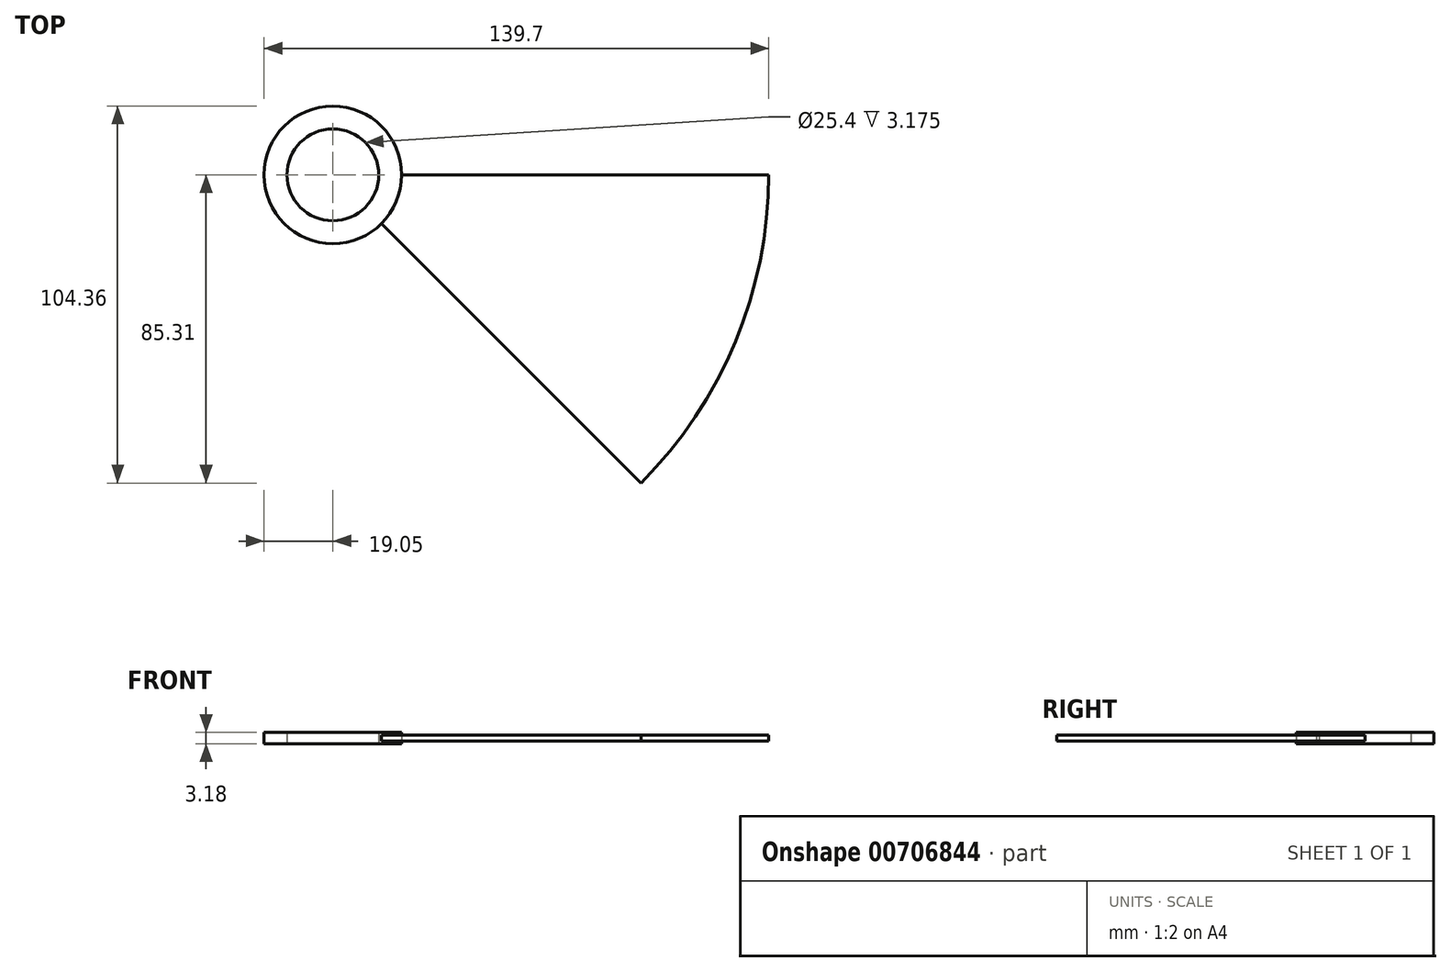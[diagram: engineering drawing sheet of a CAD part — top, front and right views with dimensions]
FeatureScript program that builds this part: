
annotation { "Feature Type Name" : "Feature", "Feature Type Description" : "" }
export const myFeature = defineFeature(function(context is Context, id is Id, definition is map)
    precondition{}
    {
        {
            var Q0;
            Q0=qCreatedBy(makeId("Top.planeOp"),FACE);
            var sketch = newSketch(context, id + "F0", { "sketchPlane" : qUnion([Q0])});
            skCircle(sketch, "E0", {"center": v(0, 0) * mm, "radius": 12.7 * mm});
            skCircle(sketch, "E1", {"center": v(0, 0) * mm, "radius": 19.05 * mm});
            skLineSegment(sketch, "E2", {"start": v(0, 0) * mm, "end": v(13.47, -13.47) * mm, "construction": true});
            skLineSegment(sketch, "E3", {"start": v(13.47, -13.47) * mm, "end": v(85.31, -85.31) * mm});
            skLineSegment(sketch, "E4", {"start": v(0, 0) * mm, "end": v(19.05, 0) * mm, "construction": true});
            skLineSegment(sketch, "E5", {"start": v(19.05, 0) * mm, "end": v(120.65, 0) * mm});
            skCircle(sketch, "E6.0", {"center": v(0, 0) * mm, "radius": 15.88 * mm});
            skArc(sketch, "E7", {"start": v(85.31, -85.31) * mm, "mid": v(86.43, -84.18) * mm, "end": v(87.53, -83.04) * mm});
            skLineSegment(sketch, "E8", {"start": v(15.52, -11.04) * mm, "end": v(87.53, -83.04) * mm});
            skLineSegment(sketch, "E9", {"start": v(18.78, -3.18) * mm, "end": v(120.6, -3.17) * mm});
            skLineSegment(sketch, "E10", {"start": v(69.85, 0) * mm, "end": v(69.85, -3.17) * mm, "construction": true});
            skPoint(sketch, "E10.endSnap0", {"position": v(69.7, -3.17) * mm});
            skLineSegment(sketch, "E11", {"start": v(51.53, -51.53) * mm, "end": v(53.88, -49.4) * mm});
            skPoint(sketch, "E11.startSnap0", {"position": v(51.53, -47.04) * mm});
            skPoint(sketch, "E11.endSnap0", {"position": v(49.4, -49.4) * mm});
            skArc(sketch, "E12", {"start": v(120.6, -3.17) * mm, "mid": v(120.64, -1.59) * mm, "end": v(120.65, 0) * mm});
            skArc(sketch, "E13", {"start": v(87.53, -83.04) * mm, "mid": v(111.47, -46.17) * mm, "end": v(120.6, -3.17) * mm});
            skSolve(sketch);
        }
        {
            var Q0;
            Q0=makeQuery(id+"F0.imprint","IMPRINT",FACE,{"disambiguationData":[TD([[makeQuery(id+"F0.imprint","IMPRINT",EDGE,{"derivedFrom":sQuery(id+"F0.wireOp",EDGE,"E6.0")}),-1.0]])]});
            var Q1;
            Q1=makeQuery(id+"F0.imprint","IMPRINT",FACE,{"disambiguationData":[TD([[makeQuery(id+"F0.imprint","IMPRINT",EDGE,{"derivedFrom":sQuery(id+"F0.wireOp",EDGE,"E0")}),-1.0]])]});
            extrude(context, id + "F1", {"entities" : qUnion([Q0, Q1]), "endBound" : BoundingType.SYMMETRIC, "depth" : 3.17 * mm, "offsetDistance" : 25.4 * mm});
        }
        {
            var Q0;
            {var subQ5=sQuery(id+"F0.wireOp",EDGE,"E11");Q0=makeQuery(id+"F0.imprint","IMPRINT",FACE,{"disambiguationData":[TD([[makeQuery(id+"F0.imprint","IMPRINT",EDGE,{"derivedFrom":subQ5}),1.0]])]});}
            var Q1;
            {var subQ0=sQuery(id+"F0.wireOp",EDGE,"E5");Q1=makeQuery(id+"F0.imprint","IMPRINT",FACE,{"disambiguationData":[TD([[makeQuery(id+"F0.imprint","IMPRINT",EDGE,{"derivedFrom":subQ0}),-1.0]])]});}
            var Q2;
            {var subQ0=sQuery(id+"F0.wireOp",EDGE,"E9");Q2=makeQuery(id+"F0.imprint","IMPRINT",FACE,{"disambiguationData":[TD([[makeQuery(id+"F0.imprint","IMPRINT",EDGE,{"derivedFrom":subQ0}),-1.0]])]});}
            var Q3;
            {var subQ0=sQuery(id+"F0.wireOp",EDGE,"E7");Q3=makeQuery(id+"F0.imprint","IMPRINT",FACE,{"disambiguationData":[TD([[makeQuery(id+"F0.imprint","IMPRINT",EDGE,{"derivedFrom":subQ0}),1.0]])]});}
            extrude(context, id + "F2", {"entities" : qUnion([Q0, Q1, Q2, Q3]), "endBound" : BoundingType.SYMMETRIC, "depth" : 1.59 * mm, "offsetDistance" : 25.4 * mm});
        }
    });
